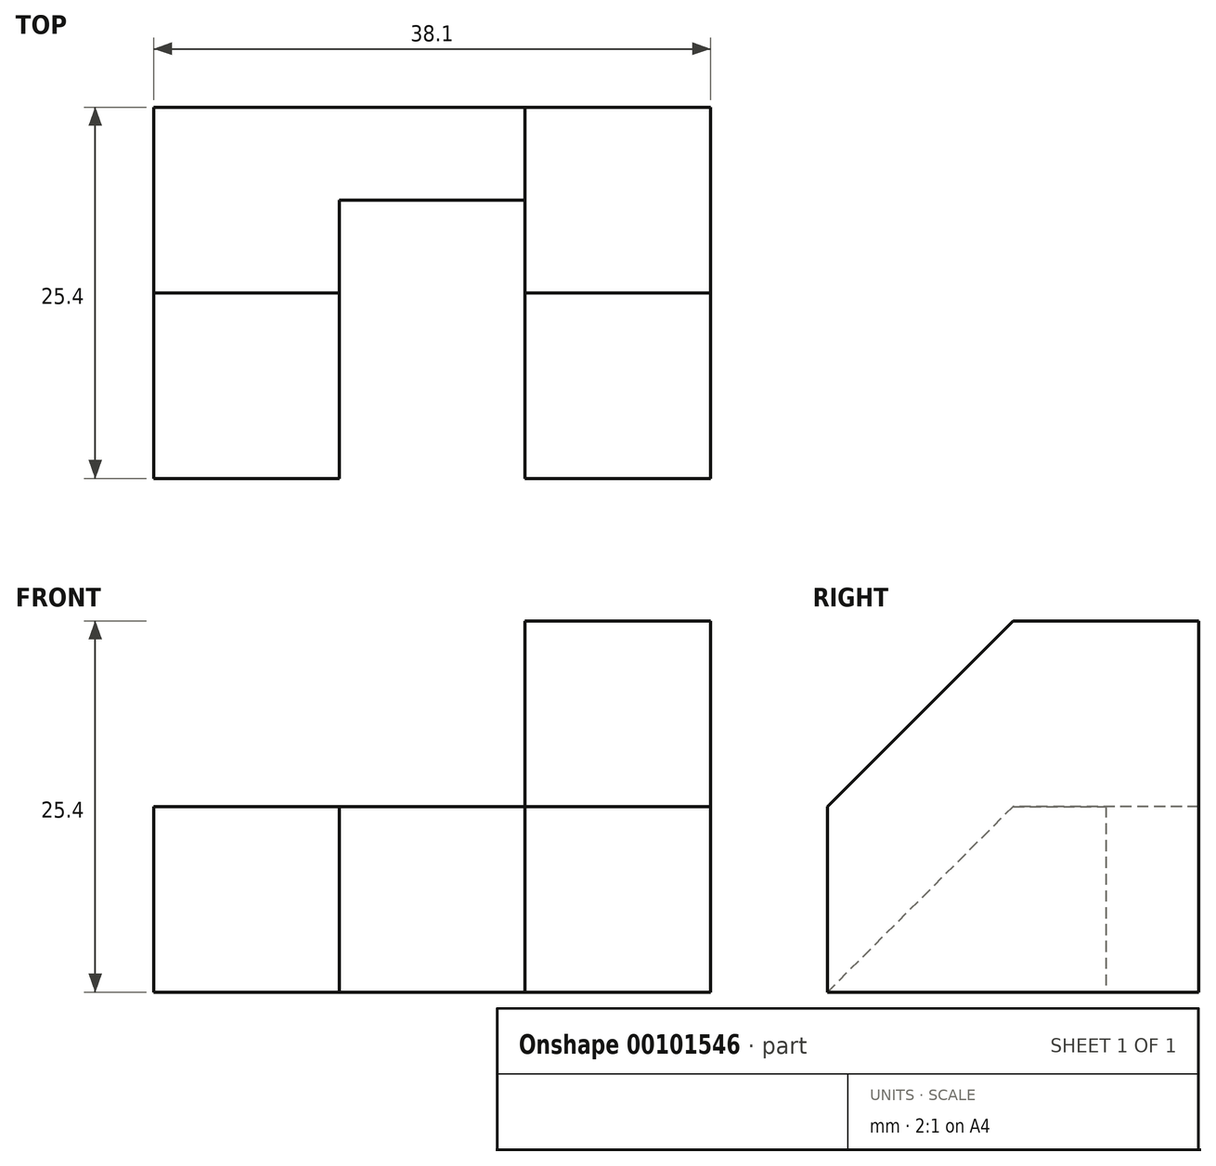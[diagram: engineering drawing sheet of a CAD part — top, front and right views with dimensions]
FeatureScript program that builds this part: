
annotation { "Feature Type Name" : "Feature", "Feature Type Description" : "" }
export const myFeature = defineFeature(function(context is Context, id is Id, definition is map)
    precondition{}
    {
        {
            var Q0;
            Q0=qCreatedBy(makeId("Right.planeOp"),FACE);
            var sketch = newSketch(context, id + "F0", { "sketchPlane" : qUnion([Q0])});
            skLineSegment(sketch, "E0", {"start": v(0, 0) * mm, "end": v(25.4, 0) * mm});
            skLineSegment(sketch, "E1", {"start": v(25.4, 0) * mm, "end": v(25.4, 25.4) * mm});
            skLineSegment(sketch, "E2", {"start": v(25.4, 25.4) * mm, "end": v(0, 25.4) * mm});
            skLineSegment(sketch, "E3", {"start": v(0, 25.4) * mm, "end": v(0, 0) * mm});
            skSolve(sketch);
        }
        {
            var Q0;
            Q0 = qSketchRegion(id + "F0", true);
            extrude(context, id + "F1", {"entities" : qUnion([Q0]), "depth" : 12.7 * mm});
        }
        {
            var Q0;
            Q0=makeQuery(id+"F1.opExtrude","CAP_FACE",FACE,{"disambiguationData":[OSD([sQuery(id+"F0.wireOp",EDGE,"E0"),sQuery(id+"F0.wireOp",EDGE,"E1"),sQuery(id+"F0.wireOp",EDGE,"E2"),sQuery(id+"F0.wireOp",EDGE,"E3")])],"isStart":false});
            var sketch = newSketch(context, id + "F2", { "sketchPlane" : qUnion([Q0])});
            skLineSegment(sketch, "E4", {"start": v(12.7, 25.4) * mm, "end": v(0, 12.7) * mm});
            skSolve(sketch);
        }
        {
            var Q0;
            Q0 = qSketchRegion(id + "F2", true);
            var Q1;
            {var subQ0=sQuery(id+"F2.wireOp",EDGE,"E4");Q1=makeQuery(id+"F2.imprint","IMPRINT",FACE,{"disambiguationData":[TD([[makeQuery(id+"F2.imprint","IMPRINT",EDGE,{"derivedFrom":subQ0}),-1.0]])]});}
            extrude(context, id + "F3", {"entities" : qUnion([Q0, Q1]), "operationType" : NewBodyOperationType.REMOVE, "endBound" : BoundingType.THROUGH_ALL, "oppositeDirection" : true, "depth" : 25.4 * mm});
        }
        {
            var Q0;
            Q0=qCreatedBy(makeId("Top.planeOp"),FACE);
            var sketch = newSketch(context, id + "F4", { "sketchPlane" : qUnion([Q0])});
            skLineSegment(sketch, "E5", {"start": v(0, 25.4) * mm, "end": v(-25.4, 25.4) * mm});
            skLineSegment(sketch, "E6", {"start": v(-25.4, 25.4) * mm, "end": v(-25.4, 0) * mm});
            skLineSegment(sketch, "E7", {"start": v(-25.4, 0) * mm, "end": v(-12.7, 0) * mm});
            skLineSegment(sketch, "E8", {"start": v(-12.7, 0) * mm, "end": v(-12.7, 19.05) * mm});
            skLineSegment(sketch, "E9", {"start": v(-12.7, 19.05) * mm, "end": v(0, 19.05) * mm});
            skLineSegment(sketch, "E10", {"start": v(0, 25.4) * mm, "end": v(0, 19.05) * mm});
            skSolve(sketch);
        }
        {
            var Q0;
            Q0=makeQuery(id+"F4.imprint","IMPRINT",FACE,{"disambiguationData":[TD([[makeQuery(id+"F4.imprint","IMPRINT",EDGE,{"derivedFrom":sQuery(id+"F4.wireOp",EDGE,"E5")}),1.0]])]});
            extrude(context, id + "F5", {"entities" : qUnion([Q0]), "operationType" : NewBodyOperationType.ADD, "depth" : 12.7 * mm});
        }
        {
            var Q0;
            Q0=makeQuery(id+"F5.opExtrude","SWEPT_FACE",FACE,{"disambiguationData":[OSD([sQuery(id+"F4.wireOp",EDGE,"E6")])]});
            var sketch = newSketch(context, id + "F6", { "sketchPlane" : qUnion([Q0])});
            skLineSegment(sketch, "E11", {"start": v(-12.7, 12.7) * mm, "end": v(0, 0) * mm});
            skSolve(sketch);
        }
        {
            var Q0;
            {var subQ0=sQuery(id+"F6.wireOp",EDGE,"E11");Q0=makeQuery(id+"F6.imprint","IMPRINT",FACE,{"disambiguationData":[TD([[makeQuery(id+"F6.imprint","IMPRINT",EDGE,{"derivedFrom":subQ0}),1.0]])]});}
            extrude(context, id + "F7", {"entities" : qUnion([Q0]), "operationType" : NewBodyOperationType.REMOVE, "oppositeDirection" : true, "depth" : 12.7 * mm});
        }
    });
